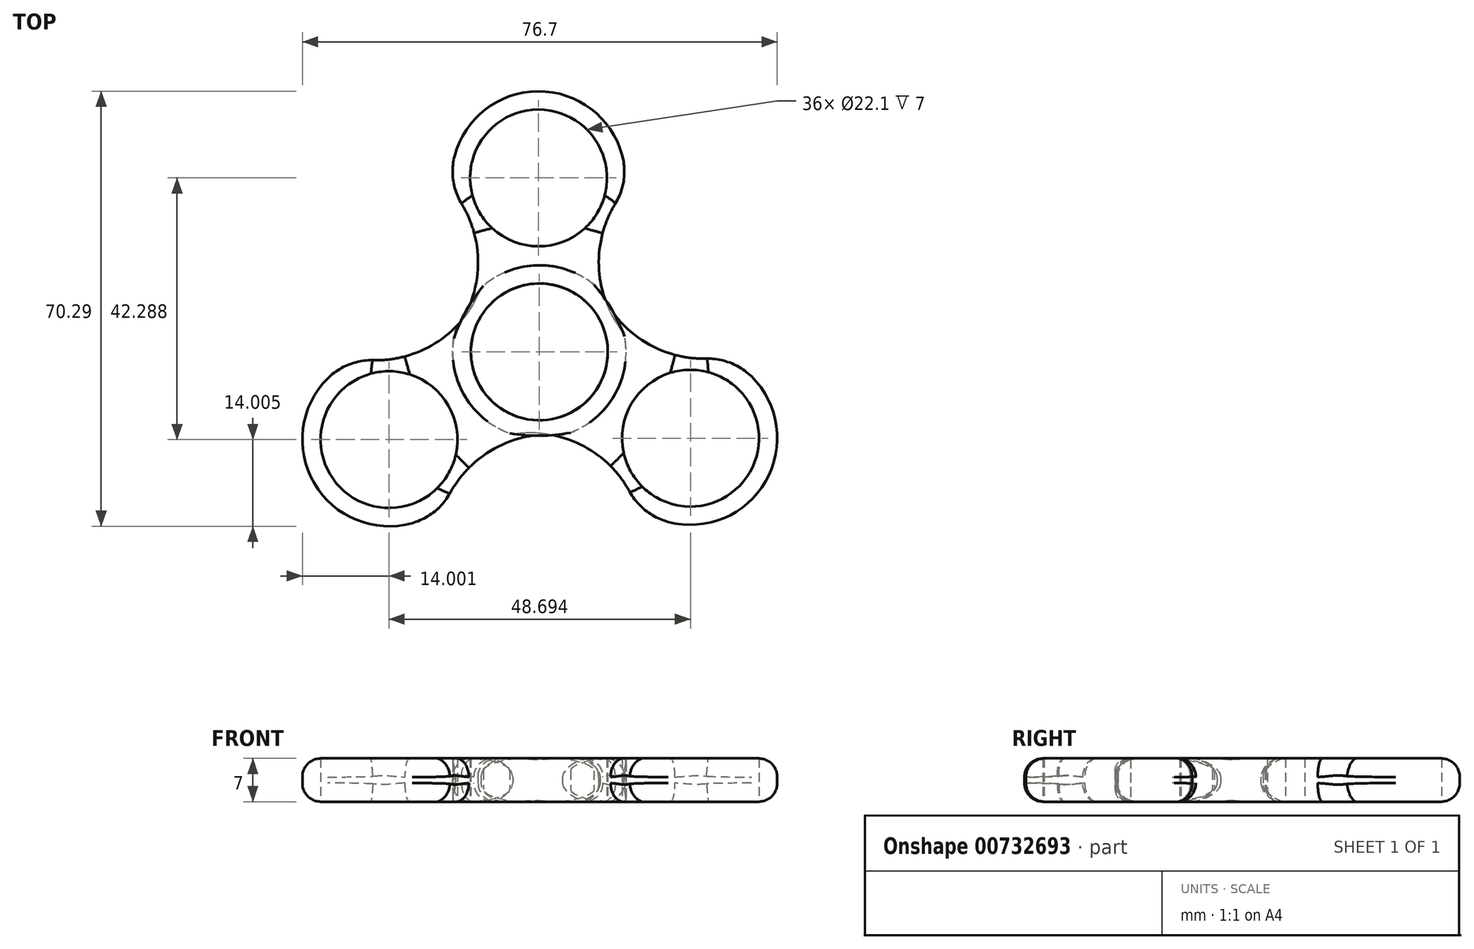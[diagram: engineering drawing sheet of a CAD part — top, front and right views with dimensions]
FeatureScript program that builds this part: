
annotation { "Feature Type Name" : "Feature", "Feature Type Description" : "" }
export const myFeature = defineFeature(function(context is Context, id is Id, definition is map)
    precondition{}
    {
        {
            var Q0;
            Q0=qCreatedBy(makeId("Top.planeOp"),FACE);
            var sketch = newSketch(context, id + "F0", { "sketchPlane" : qUnion([Q0])});
            skLineSegment(sketch, "E0.bottom", {"start": v(14.15, -14.45) * mm, "end": v(-13.85, -14.45) * mm});
            skLineSegment(sketch, "E0.top", {"start": v(14.01, 13.66) * mm, "end": v(-13.99, 13.66) * mm});
            skPoint(sketch, "E0.middle", {"position": v(0.08, -0.4) * mm});
            skCircle(sketch, "E1", {"center": v(0.01, 13.66) * mm, "radius": 14 * mm});
            skCircle(sketch, "E2", {"center": v(0.01, 13.66) * mm, "radius": 11.05 * mm});
            skCircle(sketch, "E3", {"center": v(0.15, -14.45) * mm, "radius": 14 * mm});
            skCircle(sketch, "E4", {"center": v(0.15, -14.45) * mm, "radius": 11.05 * mm});
            skCircle(sketch, "E5", {"center": v(0, 0) * mm, "radius": 28 * mm});
            skCircle(sketch, "E6", {"center": v(28, 0) * mm, "radius": 18.25 * mm});
            skCircle(sketch, "E7", {"center": v(-28, 0) * mm, "radius": 18.25 * mm});
            skSolve(sketch);
        }
        {
            var Q0;
            {var subQ4=sQuery(id+"F0.wireOp",EDGE,"E1");var subQ7=sQuery(id+"F0.wireOp",EDGE,"b9f117b0-99b1-4af1-9e43-0c6ccd36690e");var subQ9=makeQuery(id+"F0.imprint","INTERSECT",VERTEX,{"derivedFrom":[subQ4,subQ7]});Q0=makeQuery(id+"F0.imprint","IMPRINT",FACE,{"disambiguationData":[TD([[makeQuery(id+"F0.imprint","IMPRINT",EDGE,{"disambiguationData":[TD([[subQ9,-1.0]])],"derivedFrom":subQ4}),1.0]])]});}
            var Q1;
            {var subQ0=sQuery(id+"F0.wireOp",EDGE,"E1");var subQ3=sQuery(id+"F0.wireOp",EDGE,"0b0db399-f2f7-4e72-9751-79d09c067206");var subQ5=makeQuery(id+"F0.imprint","INTERSECT",VERTEX,{"derivedFrom":[subQ0,subQ3]});Q1=makeQuery(id+"F0.imprint","IMPRINT",FACE,{"disambiguationData":[TD([[makeQuery(id+"F0.imprint","IMPRINT",EDGE,{"disambiguationData":[TD([[subQ5,-1.0]])],"derivedFrom":subQ0}),1.0]])]});}
            var Q2;
            {var subQ0=sQuery(id+"F0.wireOp",EDGE,"E1");var subQ1=sQuery(id+"F0.wireOp",EDGE,"E0.top");var subQ2=makeQuery(id+"F0.imprint","INTERSECT",VERTEX,{"derivedFrom":[subQ1,sQuery(id+"F0.wireOp",EDGE,"E0.left"),subQ0]});Q2=makeQuery(id+"F0.imprint","IMPRINT",FACE,{"disambiguationData":[TD([[makeQuery(id+"F0.imprint","IMPRINT",EDGE,{"disambiguationData":[TD([[subQ2,-1.0]])],"derivedFrom":subQ1}),-1.0]])]});}
            var Q3;
            {var subQ0=sQuery(id+"F0.wireOp",EDGE,"E1");var subQ3=sQuery(id+"F0.wireOp",EDGE,"b9f117b0-99b1-4af1-9e43-0c6ccd36690e");var subQ5=makeQuery(id+"F0.imprint","INTERSECT",VERTEX,{"derivedFrom":[subQ0,subQ3]});Q3=makeQuery(id+"F0.imprint","IMPRINT",FACE,{"disambiguationData":[TD([[makeQuery(id+"F0.imprint","IMPRINT",EDGE,{"disambiguationData":[TD([[subQ5,1.0]])],"derivedFrom":subQ0}),1.0]])]});}
            var Q4;
            {var subQ0=sQuery(id+"F0.wireOp",EDGE,"E3");var subQ3=sQuery(id+"F0.wireOp",EDGE,"b9f117b0-99b1-4af1-9e43-0c6ccd36690e");var subQ5=makeQuery(id+"F0.imprint","INTERSECT",VERTEX,{"derivedFrom":[subQ0,subQ3]});Q4=makeQuery(id+"F0.imprint","IMPRINT",FACE,{"disambiguationData":[TD([[makeQuery(id+"F0.imprint","IMPRINT",EDGE,{"disambiguationData":[TD([[subQ5,-1.0]])],"derivedFrom":subQ0}),1.0]])]});}
            var Q5;
            {var subQ4=sQuery(id+"F0.wireOp",EDGE,"E3");var subQ8=makeQuery(id+"F0.imprint","INTERSECT",VERTEX,{"derivedFrom":[sQuery(id+"F0.wireOp",EDGE,"E1"),subQ4]});Q5=makeQuery(id+"F0.imprint","IMPRINT",FACE,{"disambiguationData":[TD([[makeQuery(id+"F0.imprint","IMPRINT",EDGE,{"disambiguationData":[TD([[subQ8,1.0]])],"derivedFrom":subQ4}),1.0]])]});}
            var Q6;
            {var subQ0=sQuery(id+"F0.wireOp",EDGE,"E3");var subQ3=sQuery(id+"F0.wireOp",EDGE,"0b0db399-f2f7-4e72-9751-79d09c067206");var subQ5=makeQuery(id+"F0.imprint","INTERSECT",VERTEX,{"derivedFrom":[subQ0,subQ3]});Q6=makeQuery(id+"F0.imprint","IMPRINT",FACE,{"disambiguationData":[TD([[makeQuery(id+"F0.imprint","IMPRINT",EDGE,{"disambiguationData":[TD([[subQ5,1.0]])],"derivedFrom":subQ0}),1.0]])]});}
            var Q7;
            {var subQ0=sQuery(id+"F0.wireOp",EDGE,"E3");var subQ1=sQuery(id+"F0.wireOp",EDGE,"E0.bottom");var subQ2=makeQuery(id+"F0.imprint","INTERSECT",VERTEX,{"derivedFrom":[subQ1,sQuery(id+"F0.wireOp",EDGE,"E0.left"),subQ0]});Q7=makeQuery(id+"F0.imprint","IMPRINT",FACE,{"disambiguationData":[TD([[makeQuery(id+"F0.imprint","IMPRINT",EDGE,{"disambiguationData":[TD([[subQ2,-1.0]])],"derivedFrom":subQ1}),1.0]])]});}
            var Q8;
            {var subQ0=sQuery(id+"F0.wireOp",EDGE,"E7");var subQ1=sQuery(id+"F0.wireOp",EDGE,"E1");var subQ2=makeQuery(id+"F0.imprint","INTERSECT",VERTEX,{"disambiguationData":[OD(1.0)],"derivedFrom":[subQ1,subQ0]});Q8=makeQuery(id+"F0.imprint","IMPRINT",FACE,{"disambiguationData":[TD([[makeQuery(id+"F0.imprint","IMPRINT",EDGE,{"disambiguationData":[TD([[subQ2,-1.0]])],"derivedFrom":subQ1}),-1.0]])]});}
            extrude(context, id + "F1", {"entities" : qUnion([Q0, Q1, Q2, Q3, Q4, Q5, Q6, Q7, Q8]), "depth" : 7 * mm, "offsetDistance" : 25 * mm});
        }
        {
            var Q0;
            Q0=makeQuery(id+"F1.opExtrude","SWEPT_BODY",BODY,{"disambiguationData":[OSD([sQuery(id+"F0.wireOp",EDGE,"E1"),sQuery(id+"F0.wireOp",EDGE,"E2"),sQuery(id+"F0.wireOp",EDGE,"E3"),sQuery(id+"F0.wireOp",EDGE,"E4"),sQuery(id+"F0.wireOp",EDGE,"E5"),sQuery(id+"F0.wireOp",EDGE,"E6"),sQuery(id+"F0.wireOp",EDGE,"E7")])]});
            var Q1;
            {var subQ0=sQuery(id+"F0.wireOp",EDGE,"E3");var subQ1=makeQuery(id+"F0.imprint","INTERSECT",VERTEX,{"disambiguationData":[OD(0.0)],"derivedFrom":[sQuery(id+"F0.wireOp",EDGE,"E0.bottom"),subQ0]});Q1=makeQuery(id+"F1.opExtrude","SWEPT_FACE",FACE,{"disambiguationData":[OSD([subQ0]),TDD([makeQuery(id+"F0.imprint","IMPRINT",EDGE,{"disambiguationData":[TD([[subQ1,-1.0]])],"derivedFrom":subQ0}),makeQuery(id+"F0.imprint","IMPRINT",EDGE,{"disambiguationData":[TD([[subQ1,1.0]])],"derivedFrom":subQ0})])]});}
            circularPattern(context, id + "F2", {"entities" : qUnion([Q0]), "axis" : qUnion([Q1]), "angle" : 360 * degree, "instanceCount" : 3, "equalSpace" : true});
        }
        {
            var Q0;
            Q0=makeQuery(id+"F1.opExtrude","SWEPT_EDGE",EDGE,{"disambiguationData":[OSD([sQuery(id+"F0.wireOp",EDGE,"E1"),sQuery(id+"F0.wireOp",EDGE,"E6")])]});
            var Q1;
            Q1=makeQuery(id+"F1.opExtrude","SWEPT_EDGE",EDGE,{"disambiguationData":[OSD([sQuery(id+"F0.wireOp",EDGE,"E1"),sQuery(id+"F0.wireOp",EDGE,"E7")])]});
            var Q2;
            Q2=makeQuery(id+"F2.opPattern","COPY",EDGE,{"derivedFrom":makeQuery(id+"F1.opExtrude","SWEPT_EDGE",EDGE,{"disambiguationData":[OSD([sQuery(id+"F0.wireOp",EDGE,"E1"),sQuery(id+"F0.wireOp",EDGE,"E6")])]}),"instanceName":"2"});
            var Q3;
            Q3=makeQuery(id+"F2.opPattern","COPY",EDGE,{"derivedFrom":makeQuery(id+"F1.opExtrude","SWEPT_EDGE",EDGE,{"disambiguationData":[OSD([sQuery(id+"F0.wireOp",EDGE,"E1"),sQuery(id+"F0.wireOp",EDGE,"E7")])]}),"instanceName":"2"});
            var Q4;
            Q4=makeQuery(id+"F2.opPattern","COPY",EDGE,{"derivedFrom":makeQuery(id+"F1.opExtrude","SWEPT_EDGE",EDGE,{"disambiguationData":[OSD([sQuery(id+"F0.wireOp",EDGE,"E1"),sQuery(id+"F0.wireOp",EDGE,"E6")])]}),"instanceName":"1"});
            var Q5;
            Q5=makeQuery(id+"F2.opPattern","COPY",EDGE,{"derivedFrom":makeQuery(id+"F1.opExtrude","SWEPT_EDGE",EDGE,{"disambiguationData":[OSD([sQuery(id+"F0.wireOp",EDGE,"E1"),sQuery(id+"F0.wireOp",EDGE,"E7")])]}),"instanceName":"1"});
            fillet(context, id + "F3", {"entities" : qUnion([Q0, Q1, Q2, Q3, Q4, Q5]), "radius" : 10 * mm, "tangentPropagation" : true, "allowEdgeOverflow" : false});
        }
        {
            var Q0;
            Q0=makeQuery(id+"F1.opExtrude","CAP_EDGE",EDGE,{"disambiguationData":[OSD([sQuery(id+"F0.wireOp",EDGE,"E7")])],"isStart":false});
            var Q1;
            {var subQ0=sQuery(id+"F0.wireOp",EDGE,"E7");var subQ1=sQuery(id+"F0.wireOp",EDGE,"E1");Q1=makeQuery(id+"F3.opFillet","BLEND_EDGE",EDGE,{"blendedFrom":[makeQuery(id+"F1.opExtrude","SWEPT_EDGE",EDGE,{"disambiguationData":[OSD([subQ1,subQ0])]}),makeQuery(id+"F1.opExtrude","CAP_FACE",FACE,{"disambiguationData":[OSD([subQ1,sQuery(id+"F0.wireOp",EDGE,"E2"),sQuery(id+"F0.wireOp",EDGE,"E3"),sQuery(id+"F0.wireOp",EDGE,"E4"),sQuery(id+"F0.wireOp",EDGE,"E5"),sQuery(id+"F0.wireOp",EDGE,"E6"),subQ0])],"isStart":false})],"blendedInto":[makeQuery(id+"F1.opExtrude","CAP_FACE",FACE,{"disambiguationData":[OSD([subQ1,sQuery(id+"F0.wireOp",EDGE,"E2"),sQuery(id+"F0.wireOp",EDGE,"E3"),sQuery(id+"F0.wireOp",EDGE,"E4"),sQuery(id+"F0.wireOp",EDGE,"E5"),sQuery(id+"F0.wireOp",EDGE,"E6"),subQ0])],"isStart":false})]});}
            var Q2;
            Q2=makeQuery(id+"F2.opPattern","COPY",EDGE,{"derivedFrom":makeQuery(id+"F1.opExtrude","CAP_EDGE",EDGE,{"disambiguationData":[OSD([sQuery(id+"F0.wireOp",EDGE,"E7")])],"isStart":false}),"instanceName":"1"});
            var Q3;
            Q3=makeQuery(id+"F2.opPattern","COPY",EDGE,{"derivedFrom":makeQuery(id+"F1.opExtrude","CAP_EDGE",EDGE,{"disambiguationData":[OSD([sQuery(id+"F0.wireOp",EDGE,"E7")])],"isStart":false}),"instanceName":"2"});
            fillet(context, id + "F4", {"entities" : qUnion([Q0, Q1, Q2, Q3]), "radius" : 3 * mm, "tangentPropagation" : true, "allowEdgeOverflow" : false});
        }
        {
            var Q0;
            Q0=makeQuery(id+"F1.opExtrude","CAP_EDGE",EDGE,{"disambiguationData":[OSD([sQuery(id+"F0.wireOp",EDGE,"E5")])],"isStart":false});
            var Q1;
            Q1=makeQuery(id+"F2.opPattern","COPY",EDGE,{"derivedFrom":makeQuery(id+"F1.opExtrude","CAP_EDGE",EDGE,{"disambiguationData":[OSD([sQuery(id+"F0.wireOp",EDGE,"E5")])],"isStart":false}),"instanceName":"1"});
            var Q2;
            Q2=makeQuery(id+"F2.opPattern","COPY",EDGE,{"derivedFrom":makeQuery(id+"F1.opExtrude","CAP_EDGE",EDGE,{"disambiguationData":[OSD([sQuery(id+"F0.wireOp",EDGE,"E5")])],"isStart":false}),"instanceName":"2"});
            fillet(context, id + "F5", {"entities" : qUnion([Q0, Q1, Q2]), "radius" : 2 * mm, "tangentPropagation" : true, "allowEdgeOverflow" : false});
        }
        {
            var Q0;
            Q0=makeQuery(id+"F1.opExtrude","CAP_EDGE",EDGE,{"disambiguationData":[OSD([sQuery(id+"F0.wireOp",EDGE,"E6")])],"isStart":true});
            var Q1;
            Q1=makeQuery(id+"F2.opPattern","COPY",EDGE,{"derivedFrom":makeQuery(id+"F1.opExtrude","CAP_EDGE",EDGE,{"disambiguationData":[OSD([sQuery(id+"F0.wireOp",EDGE,"E6")])],"isStart":true}),"instanceName":"2"});
            var Q2;
            Q2=makeQuery(id+"F2.opPattern","COPY",EDGE,{"derivedFrom":makeQuery(id+"F1.opExtrude","CAP_EDGE",EDGE,{"disambiguationData":[OSD([sQuery(id+"F0.wireOp",EDGE,"E6")])],"isStart":true}),"instanceName":"1"});
            fillet(context, id + "F6", {"entities" : qUnion([Q0, Q1, Q2]), "radius" : 3 * mm, "tangentPropagation" : true, "allowEdgeOverflow" : false});
        }
        {
            var Q0;
            Q0=makeQuery(id+"F2.opPattern","COPY",EDGE,{"derivedFrom":makeQuery(id+"F1.opExtrude","CAP_EDGE",EDGE,{"disambiguationData":[OSD([sQuery(id+"F0.wireOp",EDGE,"E5")])],"isStart":true}),"instanceName":"2"});
            var Q1;
            Q1=makeQuery(id+"F2.opPattern","COPY",EDGE,{"derivedFrom":makeQuery(id+"F1.opExtrude","CAP_EDGE",EDGE,{"disambiguationData":[OSD([sQuery(id+"F0.wireOp",EDGE,"E5")])],"isStart":true}),"instanceName":"1"});
            var Q2;
            Q2=makeQuery(id+"F1.opExtrude","CAP_EDGE",EDGE,{"disambiguationData":[OSD([sQuery(id+"F0.wireOp",EDGE,"E5")])],"isStart":true});
            fillet(context, id + "F7", {"entities" : qUnion([Q0, Q1, Q2]), "radius" : 2 * mm, "tangentPropagation" : true, "allowEdgeOverflow" : false});
        }
    });
